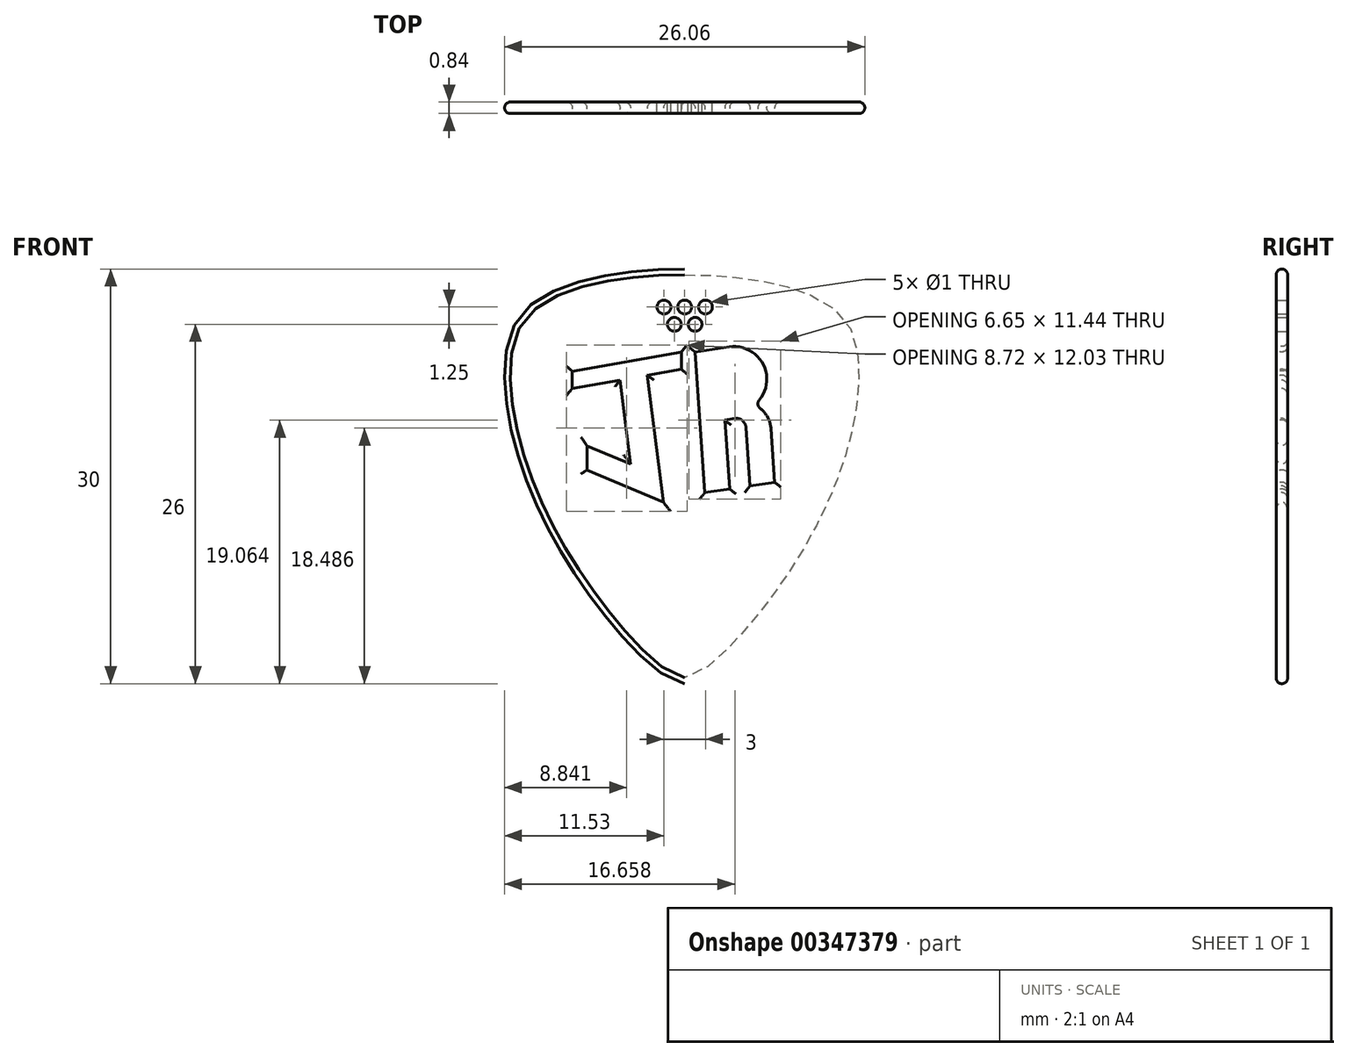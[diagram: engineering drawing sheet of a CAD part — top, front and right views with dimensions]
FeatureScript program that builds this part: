
annotation { "Feature Type Name" : "Feature", "Feature Type Description" : "" }
export const myFeature = defineFeature(function(context is Context, id is Id, definition is map)
    precondition{}
    {
        {
            var Q0;
            Q0=qCreatedBy(makeId("Front.planeOp"),FACE);
            var sketch = newSketch(context, id + "F0", { "sketchPlane" : qUnion([Q0])});
            skLineSegment(sketch, "E0", {"start": v(0, 0) * mm, "end": v(0, 6.75) * mm, "construction": true});
            skLineSegment(sketch, "E1", {"start": v(0, 0) * mm, "end": v(0, -23.25) * mm, "construction": true});
            skLineSegment(sketch, "E2", {"start": v(0, 0) * mm, "end": v(13, 0) * mm, "construction": true});
            skFitSpline(sketch, "E3", {"points": [v(0, -23.25) * mm, v(9.5, -12.75) * mm, v(13, 0) * mm, v(11, 4.25) * mm, v(0, 6.75) * mm], "startDerivative": vector(20.6, 0) * mm, "endDerivative": vector(-57.72, 0) * mm});
            skFitSpline(sketch, "E4.MirrorCS", {"points": [v(0, -23.25) * mm, v(-9.5, -12.75) * mm, v(-13, 0) * mm, v(-11, 4.25) * mm, v(0, 6.75) * mm], "startDerivative": vector(-20.6, 0) * mm, "endDerivative": vector(57.72, 0) * mm});
            skLineSegment(sketch, "E5", {"start": v(0, 2.75) * mm, "end": v(0.75, 2.75) * mm});
            skCircle(sketch, "E6", {"center": v(0.75, 2.75) * mm, "radius": 0.5 * mm});
            skLineSegment(sketch, "E7.MirrorCS", {"start": v(0, 2.75) * mm, "end": v(-0.75, 2.75) * mm});
            skCircle(sketch, "E8.MirrorC", {"center": v(-0.75, 2.75) * mm, "radius": 0.5 * mm});
            skLineSegment(sketch, "E9", {"start": v(0.75, 0.75) * mm, "end": v(1.46, -9.43) * mm});
            skLineSegment(sketch, "E10", {"start": v(1.46, -9.43) * mm, "end": v(3.24, -9.16) * mm});
            skLineSegment(sketch, "E11", {"start": v(3.24, -9.16) * mm, "end": v(2.9, -4.17) * mm});
            skLineSegment(sketch, "E12", {"start": v(2.9, -4.17) * mm, "end": v(3.63, -4.06) * mm});
            skLineSegment(sketch, "E13", {"start": v(4.73, -8.94) * mm, "end": v(4.43, -4.7) * mm});
            skLineSegment(sketch, "E14", {"start": v(3.24, -9.16) * mm, "end": v(4.73, -8.94) * mm, "construction": true});
            skLineSegment(sketch, "E15", {"start": v(4.73, -8.94) * mm, "end": v(6.5, -8.67) * mm});
            skArc(sketch, "E16", {"start": v(4.43, -4.7) * mm, "mid": v(4.17, -4.2) * mm, "end": v(3.63, -4.06) * mm});
            skLineSegment(sketch, "E17", {"start": v(6.5, -8.67) * mm, "end": v(6.23, -4.78) * mm});
            skLineSegment(sketch, "E18", {"start": v(0.75, 0.75) * mm, "end": v(3.22, 1.12) * mm});
            skArc(sketch, "E19", {"start": v(5.03, -3.08) * mm, "mid": v(5.74, -0.29) * mm, "end": v(3.22, 1.12) * mm});
            skArc(sketch, "E20", {"start": v(6.23, -4.78) * mm, "mid": v(5.87, -3.76) * mm, "end": v(5.03, -3.08) * mm});
            skLineSegment(sketch, "E21", {"start": v(-2.7, -0.93) * mm, "end": v(-1.54, -10.1) * mm});
            skLineSegment(sketch, "E22", {"start": v(-1.54, -10.1) * mm, "end": v(-7.08, -7.79) * mm});
            skLineSegment(sketch, "E23", {"start": v(-7.08, -7.79) * mm, "end": v(-7.08, -6.04) * mm});
            skLineSegment(sketch, "E24", {"start": v(-7.08, -6.04) * mm, "end": v(-3.9, -7.37) * mm});
            skLineSegment(sketch, "E25", {"start": v(-3.9, -7.37) * mm, "end": v(-4.68, -1.28) * mm});
            skLineSegment(sketch, "E26", {"start": v(-4.68, -1.28) * mm, "end": v(-8.13, -1.89) * mm});
            skLineSegment(sketch, "E27", {"start": v(-8.13, -1.89) * mm, "end": v(-8.13, -0.64) * mm});
            skLineSegment(sketch, "E28", {"start": v(-8.13, -0.64) * mm, "end": v(-0.25, 0.75) * mm});
            skLineSegment(sketch, "E29", {"start": v(-0.25, 0.75) * mm, "end": v(-0.25, -0.5) * mm});
            skLineSegment(sketch, "E30", {"start": v(-0.25, -0.5) * mm, "end": v(-2.7, -0.93) * mm});
            skLineSegment(sketch, "E31", {"start": v(-4.68, -1.28) * mm, "end": v(-2.7, -0.93) * mm, "construction": true});
            skLineSegment(sketch, "E32", {"start": v(0, 4) * mm, "end": v(1.5, 4) * mm});
            skCircle(sketch, "E33", {"center": v(0, 4) * mm, "radius": 0.5 * mm});
            skCircle(sketch, "E34", {"center": v(1.5, 4) * mm, "radius": 0.5 * mm});
            skLineSegment(sketch, "E35.MirrorCS", {"start": v(0, 4) * mm, "end": v(-1.5, 4) * mm});
            skCircle(sketch, "E36.MirrorC", {"center": v(-1.5, 4) * mm, "radius": 0.5 * mm});
            skSolve(sketch);
        }
        {
            var Q0;
            Q0=qSketchRegion(id+"F0",true);
            extrude(context, id + "F1", {"entities" : qUnion([Q0]), "depth" : 0.84 * mm});
        }
        {
            var Q0;
            Q0=makeQuery(id+"F1.opExtrude","CAP_EDGE",EDGE,{"disambiguationData":[OSD([sQuery(id+"F0.wireOp",EDGE,"E4.MirrorCS")])],"isStart":false});
            var Q1;
            Q1=makeQuery(id+"F1.opExtrude","CAP_EDGE",EDGE,{"disambiguationData":[OSD([sQuery(id+"F0.wireOp",EDGE,"E3")])],"isStart":false});
            var Q2;
            Q2=makeQuery(id+"F1.opExtrude","CAP_EDGE",EDGE,{"disambiguationData":[OSD([sQuery(id+"F0.wireOp",EDGE,"E4.MirrorCS")])],"isStart":true});
            var Q3;
            Q3=makeQuery(id+"F1.opExtrude","CAP_EDGE",EDGE,{"disambiguationData":[OSD([sQuery(id+"F0.wireOp",EDGE,"E3")])],"isStart":true});
            fillet(context, id + "F2", {"entities" : qUnion([Q0, Q1, Q2, Q3]), "radius" : 0.84 / 2 * mm, "tangentPropagation" : true, "allowEdgeOverflow" : false});
        }
        {
            var Q0;
            Q0=makeQuery(id+"F1.opExtrude","CAP_EDGE",EDGE,{"disambiguationData":[OSD([sQuery(id+"F0.wireOp",EDGE,"E24")])],"isStart":false});
            var Q1;
            Q1=makeQuery(id+"F1.opExtrude","CAP_EDGE",EDGE,{"disambiguationData":[OSD([sQuery(id+"F0.wireOp",EDGE,"E25")])],"isStart":false});
            var Q2;
            Q2=makeQuery(id+"F1.opExtrude","CAP_EDGE",EDGE,{"disambiguationData":[OSD([sQuery(id+"F0.wireOp",EDGE,"E23")])],"isStart":false});
            var Q3;
            Q3=makeQuery(id+"F1.opExtrude","CAP_EDGE",EDGE,{"disambiguationData":[OSD([sQuery(id+"F0.wireOp",EDGE,"E22")])],"isStart":false});
            var Q4;
            Q4=makeQuery(id+"F1.opExtrude","CAP_EDGE",EDGE,{"disambiguationData":[OSD([sQuery(id+"F0.wireOp",EDGE,"E21")])],"isStart":false});
            var Q5;
            Q5=makeQuery(id+"F1.opExtrude","CAP_EDGE",EDGE,{"disambiguationData":[OSD([sQuery(id+"F0.wireOp",EDGE,"E30")])],"isStart":false});
            var Q6;
            Q6=makeQuery(id+"F1.opExtrude","CAP_EDGE",EDGE,{"disambiguationData":[OSD([sQuery(id+"F0.wireOp",EDGE,"E29")])],"isStart":false});
            var Q7;
            Q7=makeQuery(id+"F1.opExtrude","CAP_EDGE",EDGE,{"disambiguationData":[OSD([sQuery(id+"F0.wireOp",EDGE,"E28")])],"isStart":false});
            var Q8;
            Q8=makeQuery(id+"F1.opExtrude","CAP_EDGE",EDGE,{"disambiguationData":[OSD([sQuery(id+"F0.wireOp",EDGE,"E27")])],"isStart":false});
            var Q9;
            Q9=makeQuery(id+"F1.opExtrude","CAP_EDGE",EDGE,{"disambiguationData":[OSD([sQuery(id+"F0.wireOp",EDGE,"E26")])],"isStart":false});
            var Q10;
            Q10=makeQuery(id+"F1.opExtrude","CAP_EDGE",EDGE,{"disambiguationData":[OSD([sQuery(id+"F0.wireOp",EDGE,"E18")])],"isStart":false});
            var Q11;
            Q11=makeQuery(id+"F1.opExtrude","CAP_EDGE",EDGE,{"disambiguationData":[OSD([sQuery(id+"F0.wireOp",EDGE,"E19")])],"isStart":false});
            var Q12;
            Q12=makeQuery(id+"F1.opExtrude","CAP_EDGE",EDGE,{"disambiguationData":[OSD([sQuery(id+"F0.wireOp",EDGE,"E9")])],"isStart":false});
            var Q13;
            Q13=makeQuery(id+"F1.opExtrude","CAP_EDGE",EDGE,{"disambiguationData":[OSD([sQuery(id+"F0.wireOp",EDGE,"E10")])],"isStart":false});
            var Q14;
            Q14=makeQuery(id+"F1.opExtrude","CAP_EDGE",EDGE,{"disambiguationData":[OSD([sQuery(id+"F0.wireOp",EDGE,"E11")])],"isStart":false});
            var Q15;
            Q15=makeQuery(id+"F1.opExtrude","CAP_EDGE",EDGE,{"disambiguationData":[OSD([sQuery(id+"F0.wireOp",EDGE,"E12")])],"isStart":false});
            var Q16;
            Q16=makeQuery(id+"F1.opExtrude","CAP_EDGE",EDGE,{"disambiguationData":[OSD([sQuery(id+"F0.wireOp",EDGE,"E15")])],"isStart":false});
            var Q17;
            Q17=makeQuery(id+"F1.opExtrude","CAP_EDGE",EDGE,{"disambiguationData":[OSD([sQuery(id+"F0.wireOp",EDGE,"E17")])],"isStart":false});
            var Q18;
            Q18=makeQuery(id+"F1.opExtrude","CAP_EDGE",EDGE,{"disambiguationData":[OSD([sQuery(id+"F0.wireOp",EDGE,"E20")])],"isStart":false});
            var Q19;
            Q19=makeQuery(id+"F1.opExtrude","CAP_EDGE",EDGE,{"disambiguationData":[OSD([sQuery(id+"F0.wireOp",EDGE,"E15")])],"isStart":true});
            var Q20;
            Q20=makeQuery(id+"F1.opExtrude","CAP_EDGE",EDGE,{"disambiguationData":[OSD([sQuery(id+"F0.wireOp",EDGE,"E13")])],"isStart":true});
            var Q21;
            Q21=makeQuery(id+"F1.opExtrude","CAP_EDGE",EDGE,{"disambiguationData":[OSD([sQuery(id+"F0.wireOp",EDGE,"E17")])],"isStart":true});
            var Q22;
            Q22=makeQuery(id+"F1.opExtrude","CAP_EDGE",EDGE,{"disambiguationData":[OSD([sQuery(id+"F0.wireOp",EDGE,"E19")])],"isStart":true});
            var Q23;
            Q23=makeQuery(id+"F1.opExtrude","CAP_EDGE",EDGE,{"disambiguationData":[OSD([sQuery(id+"F0.wireOp",EDGE,"E18")])],"isStart":true});
            var Q24;
            Q24=makeQuery(id+"F1.opExtrude","CAP_EDGE",EDGE,{"disambiguationData":[OSD([sQuery(id+"F0.wireOp",EDGE,"E9")])],"isStart":true});
            var Q25;
            Q25=makeQuery(id+"F1.opExtrude","CAP_EDGE",EDGE,{"disambiguationData":[OSD([sQuery(id+"F0.wireOp",EDGE,"E12")])],"isStart":true});
            var Q26;
            Q26=makeQuery(id+"F1.opExtrude","CAP_EDGE",EDGE,{"disambiguationData":[OSD([sQuery(id+"F0.wireOp",EDGE,"E11")])],"isStart":true});
            var Q27;
            Q27=makeQuery(id+"F1.opExtrude","CAP_EDGE",EDGE,{"disambiguationData":[OSD([sQuery(id+"F0.wireOp",EDGE,"E10")])],"isStart":true});
            var Q28;
            Q28=makeQuery(id+"F1.opExtrude","CAP_EDGE",EDGE,{"disambiguationData":[OSD([sQuery(id+"F0.wireOp",EDGE,"E21")])],"isStart":true});
            var Q29;
            Q29=makeQuery(id+"F1.opExtrude","CAP_EDGE",EDGE,{"disambiguationData":[OSD([sQuery(id+"F0.wireOp",EDGE,"E22")])],"isStart":true});
            var Q30;
            Q30=makeQuery(id+"F1.opExtrude","CAP_EDGE",EDGE,{"disambiguationData":[OSD([sQuery(id+"F0.wireOp",EDGE,"E23")])],"isStart":true});
            var Q31;
            Q31=makeQuery(id+"F1.opExtrude","CAP_EDGE",EDGE,{"disambiguationData":[OSD([sQuery(id+"F0.wireOp",EDGE,"E24")])],"isStart":true});
            var Q32;
            Q32=makeQuery(id+"F1.opExtrude","CAP_EDGE",EDGE,{"disambiguationData":[OSD([sQuery(id+"F0.wireOp",EDGE,"E25")])],"isStart":true});
            var Q33;
            Q33=makeQuery(id+"F1.opExtrude","CAP_EDGE",EDGE,{"disambiguationData":[OSD([sQuery(id+"F0.wireOp",EDGE,"E26")])],"isStart":true});
            var Q34;
            Q34=makeQuery(id+"F1.opExtrude","CAP_EDGE",EDGE,{"disambiguationData":[OSD([sQuery(id+"F0.wireOp",EDGE,"E27")])],"isStart":true});
            var Q35;
            Q35=makeQuery(id+"F1.opExtrude","CAP_EDGE",EDGE,{"disambiguationData":[OSD([sQuery(id+"F0.wireOp",EDGE,"E28")])],"isStart":true});
            var Q36;
            Q36=makeQuery(id+"F1.opExtrude","CAP_EDGE",EDGE,{"disambiguationData":[OSD([sQuery(id+"F0.wireOp",EDGE,"E30")])],"isStart":true});
            var Q37;
            Q37=makeQuery(id+"F1.opExtrude","CAP_EDGE",EDGE,{"disambiguationData":[OSD([sQuery(id+"F0.wireOp",EDGE,"E29")])],"isStart":true});
            var Q38;
            Q38=makeQuery(id+"F1.opExtrude","SWEPT_EDGE",EDGE,{"disambiguationData":[OSD([sQuery(id+"F0.wireOp",EDGE,"E19"),sQuery(id+"F0.wireOp",EDGE,"E20")])]});
            fillet(context, id + "F3", {"entities" : qUnion([Q0, Q1, Q2, Q3, Q4, Q5, Q6, Q7, Q8, Q9, Q10, Q11, Q12, Q13, Q14, Q15, Q16, Q17, Q18, Q19, Q20, Q21, Q22, Q23, Q24, Q25, Q26, Q27, Q28, Q29, Q30, Q31, Q32, Q33, Q34, Q35, Q36, Q37, Q38]), "radius" : (0.84 / 2) * mm, "tangentPropagation" : true, "allowEdgeOverflow" : false});
        }
    });
